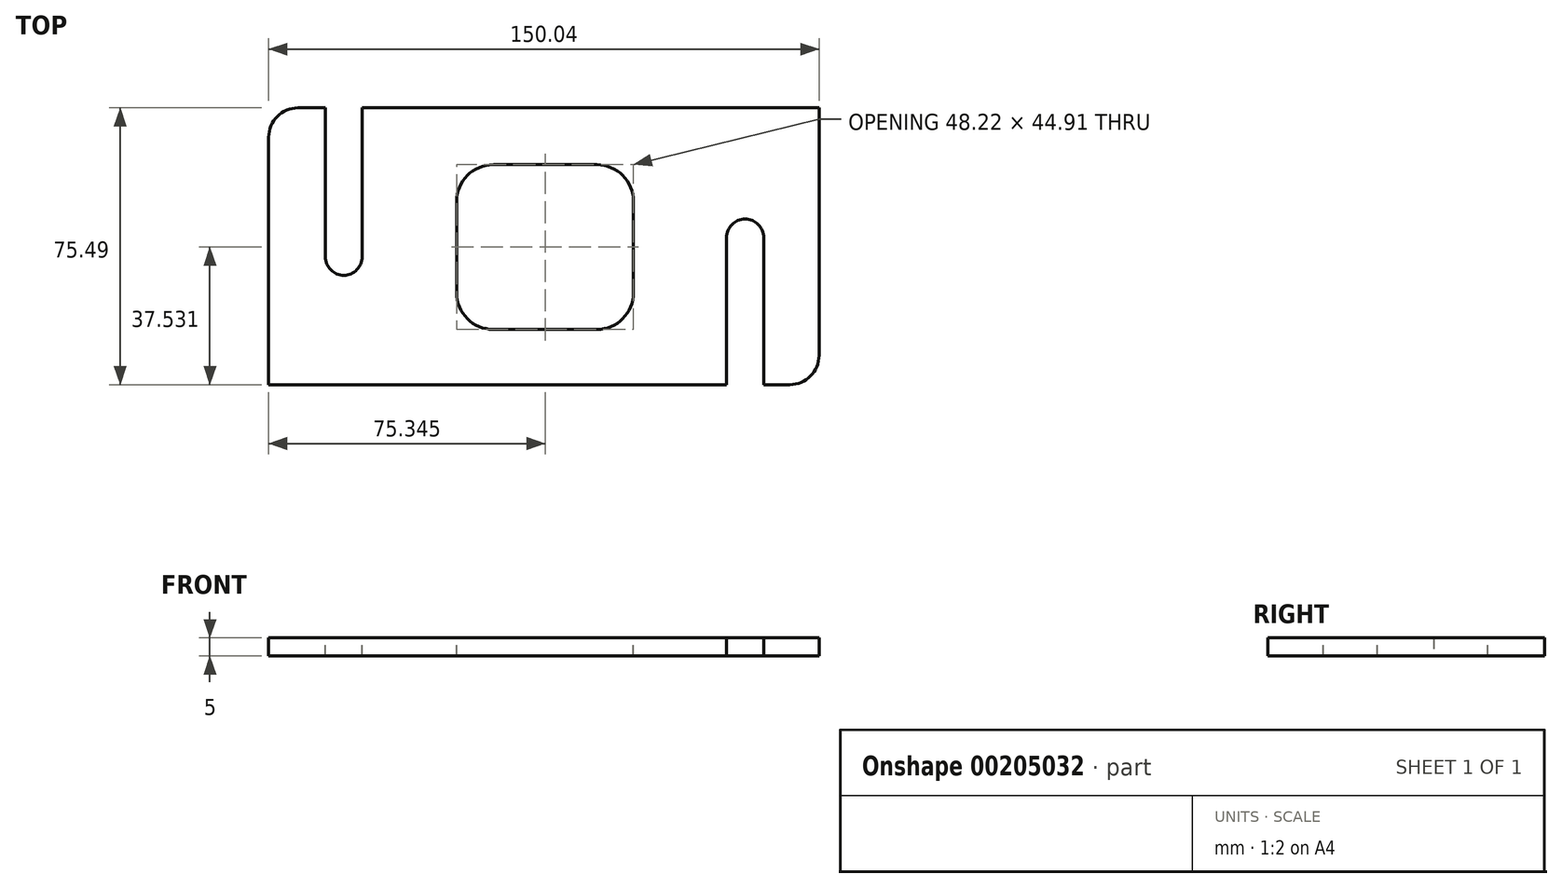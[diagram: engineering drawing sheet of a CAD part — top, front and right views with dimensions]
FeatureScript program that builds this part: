
annotation { "Feature Type Name" : "Feature", "Feature Type Description" : "" }
export const myFeature = defineFeature(function(context is Context, id is Id, definition is map)
    precondition{}
    {
        {
            var Q0;
            Q0=qCreatedBy(makeId("Top.planeOp"),FACE);
            var sketch = newSketch(context, id + "F0", { "sketchPlane" : qUnion([Q0])});
            skLineSegment(sketch, "E0.bottom", {"start": v(9.9, -7.76) * mm, "end": v(159.94, -7.76) * mm});
            skLineSegment(sketch, "E0.top", {"start": v(9.9, -83.25) * mm, "end": v(159.94, -83.25) * mm});
            skLineSegment(sketch, "E0.left", {"start": v(9.9, -7.76) * mm, "end": v(9.9, -83.25) * mm});
            skLineSegment(sketch, "E0.right", {"start": v(159.94, -7.76) * mm, "end": v(159.94, -83.25) * mm});
            skSolve(sketch);
        }
        {
            var Q0;
            Q0=makeQuery(id+"F0.imprint","IMPRINT",FACE,{"disambiguationData":[TD([[makeQuery(id+"F0.imprint","IMPRINT",EDGE,{"derivedFrom":sQuery(id+"F0.wireOp",EDGE,"E0.bottom")}),-1.0]])]});
            extrude(context, id + "F1", {"entities" : qUnion([Q0]), "depth" : 5 * mm});
        }
        {
            var Q0;
            Q0=makeQuery(id+"F1.opExtrude","CAP_FACE",FACE,{"disambiguationData":[OSD([sQuery(id+"F0.wireOp",EDGE,"E0.bottom"),sQuery(id+"F0.wireOp",EDGE,"E0.top"),sQuery(id+"F0.wireOp",EDGE,"E0.left"),sQuery(id+"F0.wireOp",EDGE,"E0.right")])],"isStart":true});
            var sketch = newSketch(context, id + "F2", { "sketchPlane" : qUnion([Q0])});
            skLineSegment(sketch, "E1.right", {"start": v(144.87, 83.25) * mm, "end": v(144.87, 78.2) * mm});
            skLineSegment(sketch, "E2.bottom", {"start": v(144.87, 83.25) * mm, "end": v(134.7, 83.25) * mm});
            skLineSegment(sketch, "E2.top", {"start": v(144.87, 43.16) * mm, "end": v(134.7, 43.16) * mm});
            skLineSegment(sketch, "E2.left", {"start": v(144.87, 78.2) * mm, "end": v(144.87, 43.16) * mm});
            skLineSegment(sketch, "E2.right", {"start": v(134.7, 83.25) * mm, "end": v(134.7, 43.16) * mm});
            skArc(sketch, "E3", {"start": v(134.7, 43.16) * mm, "mid": v(139.78, 38.08) * mm, "end": v(144.87, 43.16) * mm});
            skSolve(sketch);
        }
        {
            var Q0;
            Q0 = qSketchRegion(id + "F2", true);
            extrude(context, id + "F3", {"entities" : qUnion([Q0]), "operationType" : NewBodyOperationType.REMOVE, "oppositeDirection" : true, "depth" : 9.8 * mm});
        }
        {
            var Q0;
            Q0=makeQuery(id+"F1.opExtrude","CAP_FACE",FACE,{"disambiguationData":[OSD([sQuery(id+"F0.wireOp",EDGE,"E0.bottom"),sQuery(id+"F0.wireOp",EDGE,"E0.top"),sQuery(id+"F0.wireOp",EDGE,"E0.left"),sQuery(id+"F0.wireOp",EDGE,"E0.right")])],"isStart":false});
            var sketch = newSketch(context, id + "F4", { "sketchPlane" : qUnion([Q0])});
            skLineSegment(sketch, "E4.right", {"start": v(25.37, -7.76) * mm, "end": v(25.37, -10.52) * mm});
            skLineSegment(sketch, "E5.bottom", {"start": v(25.37, -7.76) * mm, "end": v(35.38, -7.76) * mm});
            skLineSegment(sketch, "E5.top", {"start": v(25.37, -48.4) * mm, "end": v(35.38, -48.4) * mm});
            skLineSegment(sketch, "E5.left", {"start": v(25.37, -7.76) * mm, "end": v(25.37, -48.4) * mm});
            skLineSegment(sketch, "E5.right", {"start": v(35.38, -7.76) * mm, "end": v(35.38, -48.4) * mm});
            skArc(sketch, "E6", {"start": v(25.37, -48.4) * mm, "mid": v(30.38, -53.4) * mm, "end": v(35.38, -48.4) * mm});
            skSolve(sketch);
        }
        {
            var Q0;
            Q0 = qSketchRegion(id + "F4", true);
            extrude(context, id + "F5", {"entities" : qUnion([Q0]), "operationType" : NewBodyOperationType.REMOVE, "oppositeDirection" : true, "depth" : 15.9 * mm});
        }
        {
            var Q0;
            Q0=makeQuery(id+"F1.opExtrude","CAP_FACE",FACE,{"disambiguationData":[OSD([sQuery(id+"F0.wireOp",EDGE,"E0.bottom"),sQuery(id+"F0.wireOp",EDGE,"E0.top"),sQuery(id+"F0.wireOp",EDGE,"E0.left"),sQuery(id+"F0.wireOp",EDGE,"E0.right")])],"isStart":false});
            var sketch = newSketch(context, id + "F6", { "sketchPlane" : qUnion([Q0])});
            skLineSegment(sketch, "E7.bottom", {"start": v(61.14, -23.26) * mm, "end": v(109.35, -23.26) * mm});
            skLineSegment(sketch, "E7.top", {"start": v(61.14, -68.17) * mm, "end": v(109.35, -68.17) * mm});
            skLineSegment(sketch, "E7.left", {"start": v(61.14, -23.26) * mm, "end": v(61.14, -68.17) * mm});
            skLineSegment(sketch, "E7.right", {"start": v(109.35, -23.26) * mm, "end": v(109.35, -68.17) * mm});
            skSolve(sketch);
        }
        {
            var Q0;
            Q0 = qSketchRegion(id + "F6", true);
            extrude(context, id + "F7", {"entities" : qUnion([Q0]), "operationType" : NewBodyOperationType.REMOVE, "oppositeDirection" : true, "depth" : 12.5 * mm});
        }
        {
            var Q0;
            Q0=makeQuery(id+"F7.boolean.opBoolean","COPY",EDGE,{"derivedFrom":makeQuery(id+"F7.opExtrude","SWEPT_EDGE",EDGE,{"disambiguationData":[OSD([sQuery(id+"F6.wireOp",EDGE,"E7.bottom"),sQuery(id+"F6.wireOp",EDGE,"E7.right")])]})});
            var Q1;
            Q1=makeQuery(id+"F7.boolean.opBoolean","COPY",EDGE,{"derivedFrom":makeQuery(id+"F7.opExtrude","SWEPT_EDGE",EDGE,{"disambiguationData":[OSD([sQuery(id+"F6.wireOp",EDGE,"E7.top"),sQuery(id+"F6.wireOp",EDGE,"E7.left")])]})});
            var Q2;
            Q2=makeQuery(id+"F7.boolean.opBoolean","COPY",EDGE,{"derivedFrom":makeQuery(id+"F7.opExtrude","SWEPT_EDGE",EDGE,{"disambiguationData":[OSD([sQuery(id+"F6.wireOp",EDGE,"E7.top"),sQuery(id+"F6.wireOp",EDGE,"E7.right")])]})});
            var Q3;
            Q3=makeQuery(id+"F7.boolean.opBoolean","COPY",EDGE,{"derivedFrom":makeQuery(id+"F7.opExtrude","SWEPT_EDGE",EDGE,{"disambiguationData":[OSD([sQuery(id+"F6.wireOp",EDGE,"E7.bottom"),sQuery(id+"F6.wireOp",EDGE,"E7.left")])]})});
            fillet(context, id + "F8", {"entities" : qUnion([Q0, Q1, Q2, Q3]), "radius" : 10 * mm, "tangentPropagation" : true, "allowEdgeOverflow" : false});
        }
        {
            var Q0;
            Q0=makeQuery(id+"F1.opExtrude","SWEPT_EDGE",EDGE,{"disambiguationData":[OSD([sQuery(id+"F0.wireOp",EDGE,"E0.bottom"),sQuery(id+"F0.wireOp",EDGE,"E0.left")])]});
            var Q1;
            Q1=makeQuery(id+"F1.opExtrude","SWEPT_EDGE",EDGE,{"disambiguationData":[OSD([sQuery(id+"F0.wireOp",EDGE,"E0.top"),sQuery(id+"F0.wireOp",EDGE,"E0.right")])]});
            fillet(context, id + "F9", {"entities" : qUnion([Q0, Q1]), "radius" : 8 * mm, "tangentPropagation" : true, "allowEdgeOverflow" : false});
        }
    });
